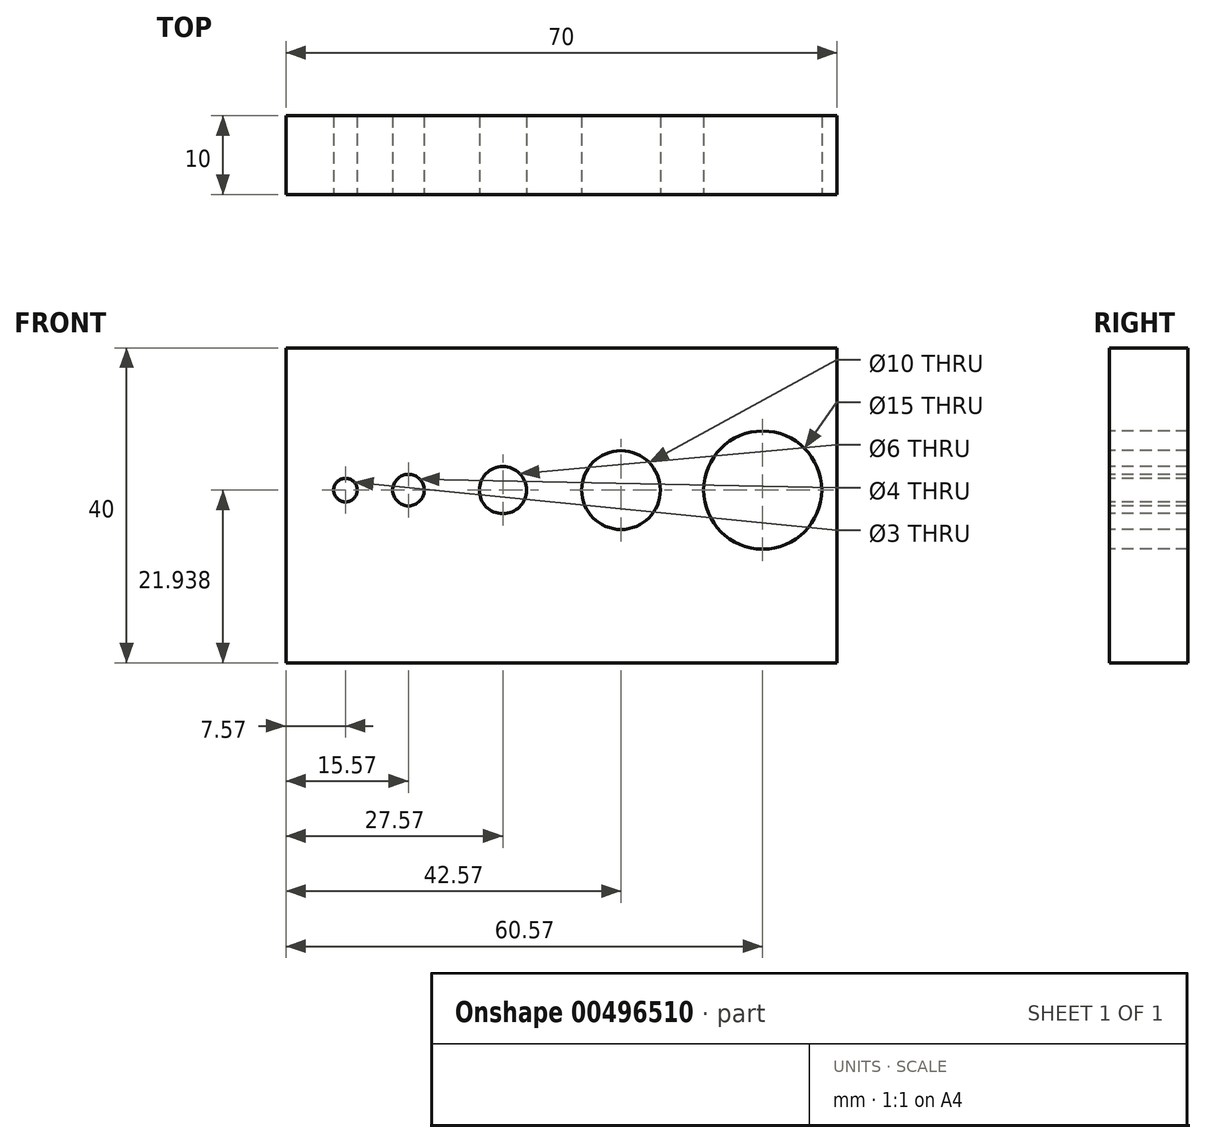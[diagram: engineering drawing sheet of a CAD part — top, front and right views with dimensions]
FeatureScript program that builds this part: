
annotation { "Feature Type Name" : "Feature", "Feature Type Description" : "" }
export const myFeature = defineFeature(function(context is Context, id is Id, definition is map)
    precondition{}
    {
        {
            var Q0;
            Q0=qCreatedBy(makeId("Top.planeOp"),FACE);
            var sketch = newSketch(context, id + "F0", { "sketchPlane" : qUnion([Q0])});
            skLineSegment(sketch, "E0.bottom", {"start": v(-35, 5) * mm, "end": v(35, 5) * mm});
            skLineSegment(sketch, "E0.top", {"start": v(-35, -5) * mm, "end": v(35, -5) * mm});
            skLineSegment(sketch, "E0.left", {"start": v(-35, 5) * mm, "end": v(-35, -5) * mm});
            skLineSegment(sketch, "E0.right", {"start": v(35, 5) * mm, "end": v(35, -5) * mm});
            skSolve(sketch);
        }
        {
            var Q0;
            Q0=makeQuery(id+"F0.imprint","IMPRINT",FACE,{"disambiguationData":[TD([[makeQuery(id+"F0.imprint","IMPRINT",EDGE,{"derivedFrom":sQuery(id+"F0.wireOp",EDGE,"E0.bottom")}),-1.0]])]});
            extrude(context, id + "F1", {"entities" : qUnion([Q0]), "depth" : 40 * mm});
        }
        {
            var Q0;
            Q0=makeQuery(id+"F1.opExtrude","SWEPT_FACE",FACE,{"disambiguationData":[OSD([sQuery(id+"F0.wireOp",EDGE,"E0.top")])]});
            var sketch = newSketch(context, id + "F2", { "sketchPlane" : qUnion([Q0])});
            skPoint(sketch, "E1", {"position": v(-27.43, 21.94) * mm});
            skPoint(sketch, "E2", {"position": v(-7.43, 21.94) * mm});
            skPoint(sketch, "E3", {"position": v(25.57, 21.94) * mm});
            skPoint(sketch, "E4", {"position": v(7.57, 21.94) * mm});
            skPoint(sketch, "E5", {"position": v(-19.43, 21.94) * mm});
            skCircle(sketch, "E6", {"center": v(-27.43, 21.94) * mm, "radius": 1.5 * mm});
            skCircle(sketch, "E7", {"center": v(-19.43, 21.94) * mm, "radius": 2 * mm});
            skCircle(sketch, "E8", {"center": v(-7.43, 21.94) * mm, "radius": 3 * mm});
            skCircle(sketch, "E9", {"center": v(7.57, 21.94) * mm, "radius": 5 * mm});
            skCircle(sketch, "E10", {"center": v(25.57, 21.94) * mm, "radius": 7.5 * mm});
            skSolve(sketch);
        }
        {
            var Q0;
            Q0=makeQuery(id+"F2.imprint","IMPRINT",FACE,{"disambiguationData":[TD([[makeQuery(id+"F2.imprint","IMPRINT",EDGE,{"derivedFrom":sQuery(id+"F2.wireOp",EDGE,"E9")}),1.0]])]});
            var Q1;
            Q1=makeQuery(id+"F2.imprint","IMPRINT",FACE,{"disambiguationData":[TD([[makeQuery(id+"F2.imprint","IMPRINT",EDGE,{"derivedFrom":sQuery(id+"F2.wireOp",EDGE,"E10")}),1.0]])]});
            var Q2;
            Q2=makeQuery(id+"F2.imprint","IMPRINT",FACE,{"disambiguationData":[TD([[makeQuery(id+"F2.imprint","IMPRINT",EDGE,{"derivedFrom":sQuery(id+"F2.wireOp",EDGE,"E8")}),1.0]])]});
            var Q3;
            Q3=makeQuery(id+"F2.imprint","IMPRINT",FACE,{"disambiguationData":[TD([[makeQuery(id+"F2.imprint","IMPRINT",EDGE,{"derivedFrom":sQuery(id+"F2.wireOp",EDGE,"E7")}),1.0]])]});
            var Q4;
            Q4=makeQuery(id+"F2.imprint","IMPRINT",FACE,{"disambiguationData":[TD([[makeQuery(id+"F2.imprint","IMPRINT",EDGE,{"derivedFrom":sQuery(id+"F2.wireOp",EDGE,"E6")}),1.0]])]});
            extrude(context, id + "F3", {"entities" : qUnion([Q0, Q1, Q2, Q3, Q4]), "operationType" : NewBodyOperationType.REMOVE, "oppositeDirection" : true, "depth" : 25 * mm});
        }
    });
